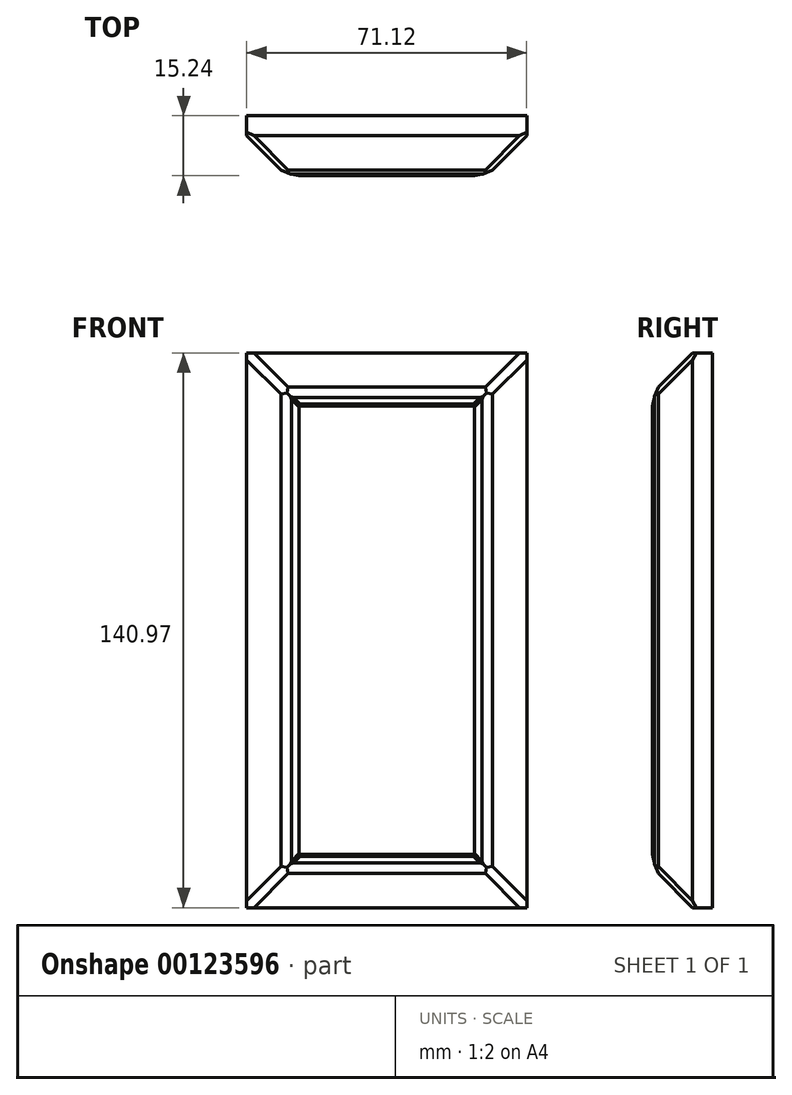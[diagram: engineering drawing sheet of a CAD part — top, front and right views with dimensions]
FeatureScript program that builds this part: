
annotation { "Feature Type Name" : "Feature", "Feature Type Description" : "" }
export const myFeature = defineFeature(function(context is Context, id is Id, definition is map)
    precondition{}
    {
        {
            var Q0;
            Q0=qCreatedBy(makeId("Front.planeOp"),FACE);
            var sketch = newSketch(context, id + "F0", { "sketchPlane" : qUnion([Q0])});
            skLineSegment(sketch, "E0.bottom", {"start": v(-36.8, 94.4) * mm, "end": v(34.31, 94.4) * mm});
            skLineSegment(sketch, "E0.top", {"start": v(-36.8, -46.57) * mm, "end": v(34.31, -46.57) * mm});
            skLineSegment(sketch, "E0.left", {"start": v(-36.8, 94.4) * mm, "end": v(-36.8, -46.57) * mm});
            skLineSegment(sketch, "E0.right", {"start": v(34.31, 94.4) * mm, "end": v(34.31, -46.57) * mm});
            skSolve(sketch);
        }
        {
            var Q0;
            Q0 = qSketchRegion(id + "F0", true);
            extrude(context, id + "F1", {"entities" : qUnion([Q0]), "depth" : 15.24 * mm});
        }
        {
            var Q0;
            Q0=makeQuery(id+"F1.opExtrude","CAP_EDGE",EDGE,{"disambiguationData":[OSD([sQuery(id+"F0.wireOp",EDGE,"E0.bottom")])],"isStart":false});
            var Q1;
            Q1=makeQuery(id+"F1.opExtrude","CAP_EDGE",EDGE,{"disambiguationData":[OSD([sQuery(id+"F0.wireOp",EDGE,"E0.right")])],"isStart":false});
            var Q2;
            Q2=makeQuery(id+"F1.opExtrude","CAP_EDGE",EDGE,{"disambiguationData":[OSD([sQuery(id+"F0.wireOp",EDGE,"E0.left")])],"isStart":false});
            var Q3;
            Q3=makeQuery(id+"F1.opExtrude","CAP_EDGE",EDGE,{"disambiguationData":[OSD([sQuery(id+"F0.wireOp",EDGE,"E0.top")])],"isStart":false});
            chamfer(context, id + "F2", {"entities" : qUnion([Q0, Q1, Q2, Q3]), "width" : 10.16 * mm, "tangentPropagation" : true});
        }
        {
            var Q0;
            {var subQ0=sQuery(id+"F0.wireOp",EDGE,"E0.left");Q0=makeQuery(id+"F2.opChamfer","BLEND_EDGE",EDGE,{"blendedFrom":[makeQuery(id+"F1.opExtrude","CAP_EDGE",EDGE,{"disambiguationData":[OSD([subQ0])],"isStart":false}),makeQuery(id+"F1.opExtrude","CAP_FACE",FACE,{"disambiguationData":[OSD([sQuery(id+"F0.wireOp",EDGE,"E0.bottom"),sQuery(id+"F0.wireOp",EDGE,"E0.top"),subQ0,sQuery(id+"F0.wireOp",EDGE,"E0.right")])],"isStart":false})],"blendedInto":[makeQuery(id+"F1.opExtrude","CAP_FACE",FACE,{"disambiguationData":[OSD([sQuery(id+"F0.wireOp",EDGE,"E0.bottom"),sQuery(id+"F0.wireOp",EDGE,"E0.top"),subQ0,sQuery(id+"F0.wireOp",EDGE,"E0.right")])],"isStart":false})]});}
            var Q1;
            {var subQ0=sQuery(id+"F0.wireOp",EDGE,"E0.top");Q1=makeQuery(id+"F2.opChamfer","BLEND_EDGE",EDGE,{"blendedFrom":[makeQuery(id+"F1.opExtrude","CAP_EDGE",EDGE,{"disambiguationData":[OSD([subQ0])],"isStart":false}),makeQuery(id+"F1.opExtrude","CAP_FACE",FACE,{"disambiguationData":[OSD([sQuery(id+"F0.wireOp",EDGE,"E0.bottom"),subQ0,sQuery(id+"F0.wireOp",EDGE,"E0.left"),sQuery(id+"F0.wireOp",EDGE,"E0.right")])],"isStart":false})],"blendedInto":[makeQuery(id+"F1.opExtrude","CAP_FACE",FACE,{"disambiguationData":[OSD([sQuery(id+"F0.wireOp",EDGE,"E0.bottom"),subQ0,sQuery(id+"F0.wireOp",EDGE,"E0.left"),sQuery(id+"F0.wireOp",EDGE,"E0.right")])],"isStart":false})]});}
            var Q2;
            {var subQ0=sQuery(id+"F0.wireOp",EDGE,"E0.right");Q2=makeQuery(id+"F2.opChamfer","BLEND_EDGE",EDGE,{"blendedFrom":[makeQuery(id+"F1.opExtrude","CAP_EDGE",EDGE,{"disambiguationData":[OSD([subQ0])],"isStart":false}),makeQuery(id+"F1.opExtrude","CAP_FACE",FACE,{"disambiguationData":[OSD([sQuery(id+"F0.wireOp",EDGE,"E0.bottom"),sQuery(id+"F0.wireOp",EDGE,"E0.top"),sQuery(id+"F0.wireOp",EDGE,"E0.left"),subQ0])],"isStart":false})],"blendedInto":[makeQuery(id+"F1.opExtrude","CAP_FACE",FACE,{"disambiguationData":[OSD([sQuery(id+"F0.wireOp",EDGE,"E0.bottom"),sQuery(id+"F0.wireOp",EDGE,"E0.top"),sQuery(id+"F0.wireOp",EDGE,"E0.left"),subQ0])],"isStart":false})]});}
            var Q3;
            {var subQ0=sQuery(id+"F0.wireOp",EDGE,"E0.bottom");Q3=makeQuery(id+"F2.opChamfer","BLEND_EDGE",EDGE,{"blendedFrom":[makeQuery(id+"F1.opExtrude","CAP_EDGE",EDGE,{"disambiguationData":[OSD([subQ0])],"isStart":false}),makeQuery(id+"F1.opExtrude","CAP_FACE",FACE,{"disambiguationData":[OSD([subQ0,sQuery(id+"F0.wireOp",EDGE,"E0.top"),sQuery(id+"F0.wireOp",EDGE,"E0.left"),sQuery(id+"F0.wireOp",EDGE,"E0.right")])],"isStart":false})],"blendedInto":[makeQuery(id+"F1.opExtrude","CAP_FACE",FACE,{"disambiguationData":[OSD([subQ0,sQuery(id+"F0.wireOp",EDGE,"E0.top"),sQuery(id+"F0.wireOp",EDGE,"E0.left"),sQuery(id+"F0.wireOp",EDGE,"E0.right")])],"isStart":false})]});}
            chamfer(context, id + "F3", {"entities" : qUnion([Q0, Q1, Q2, Q3]), "width" : 5.08 * mm, "tangentPropagation" : true});
        }
        {
            var Q0;
            {var subQ0=sQuery(id+"F0.wireOp",EDGE,"E0.bottom");var subQ1=makeQuery(id+"F1.opExtrude","CAP_FACE",FACE,{"disambiguationData":[OSD([subQ0,sQuery(id+"F0.wireOp",EDGE,"E0.top"),sQuery(id+"F0.wireOp",EDGE,"E0.left"),sQuery(id+"F0.wireOp",EDGE,"E0.right")])],"isStart":false});Q0=makeQuery(id+"F3.opChamfer","BLEND_EDGE",EDGE,{"blendedFrom":[makeQuery(id+"F2.opChamfer","BLEND_EDGE",EDGE,{"blendedFrom":[makeQuery(id+"F1.opExtrude","CAP_EDGE",EDGE,{"disambiguationData":[OSD([subQ0])],"isStart":false}),subQ1],"blendedInto":[subQ1]}),subQ1],"blendedInto":[subQ1]});}
            var Q1;
            {var subQ0=sQuery(id+"F0.wireOp",EDGE,"E0.top");var subQ1=makeQuery(id+"F1.opExtrude","CAP_FACE",FACE,{"disambiguationData":[OSD([sQuery(id+"F0.wireOp",EDGE,"E0.bottom"),subQ0,sQuery(id+"F0.wireOp",EDGE,"E0.left"),sQuery(id+"F0.wireOp",EDGE,"E0.right")])],"isStart":false});Q1=makeQuery(id+"F3.opChamfer","BLEND_EDGE",EDGE,{"blendedFrom":[makeQuery(id+"F2.opChamfer","BLEND_EDGE",EDGE,{"blendedFrom":[makeQuery(id+"F1.opExtrude","CAP_EDGE",EDGE,{"disambiguationData":[OSD([subQ0])],"isStart":false}),subQ1],"blendedInto":[subQ1]}),subQ1],"blendedInto":[subQ1]});}
            var Q2;
            {var subQ0=sQuery(id+"F0.wireOp",EDGE,"E0.left");var subQ1=makeQuery(id+"F1.opExtrude","CAP_FACE",FACE,{"disambiguationData":[OSD([sQuery(id+"F0.wireOp",EDGE,"E0.bottom"),sQuery(id+"F0.wireOp",EDGE,"E0.top"),subQ0,sQuery(id+"F0.wireOp",EDGE,"E0.right")])],"isStart":false});Q2=makeQuery(id+"F3.opChamfer","BLEND_EDGE",EDGE,{"blendedFrom":[makeQuery(id+"F2.opChamfer","BLEND_EDGE",EDGE,{"blendedFrom":[makeQuery(id+"F1.opExtrude","CAP_EDGE",EDGE,{"disambiguationData":[OSD([subQ0])],"isStart":false}),subQ1],"blendedInto":[subQ1]}),subQ1],"blendedInto":[subQ1]});}
            var Q3;
            {var subQ0=sQuery(id+"F0.wireOp",EDGE,"E0.right");var subQ1=makeQuery(id+"F1.opExtrude","CAP_FACE",FACE,{"disambiguationData":[OSD([sQuery(id+"F0.wireOp",EDGE,"E0.bottom"),sQuery(id+"F0.wireOp",EDGE,"E0.top"),sQuery(id+"F0.wireOp",EDGE,"E0.left"),subQ0])],"isStart":false});Q3=makeQuery(id+"F3.opChamfer","BLEND_EDGE",EDGE,{"blendedFrom":[makeQuery(id+"F2.opChamfer","BLEND_EDGE",EDGE,{"blendedFrom":[makeQuery(id+"F1.opExtrude","CAP_EDGE",EDGE,{"disambiguationData":[OSD([subQ0])],"isStart":false}),subQ1],"blendedInto":[subQ1]}),subQ1],"blendedInto":[subQ1]});}
            chamfer(context, id + "F4", {"entities" : qUnion([Q0, Q1, Q2, Q3]), "width" : 5.08 * mm, "tangentPropagation" : true});
        }
        {
            var Q0;
            {var subQ0=sQuery(id+"F0.wireOp",EDGE,"E0.right");var subQ1=sQuery(id+"F0.wireOp",EDGE,"E0.bottom");var subQ2=makeQuery(id+"F1.opExtrude","CAP_FACE",FACE,{"disambiguationData":[OSD([subQ1,sQuery(id+"F0.wireOp",EDGE,"E0.top"),sQuery(id+"F0.wireOp",EDGE,"E0.left"),subQ0])],"isStart":false});var subQ3=subQ2;Q0=makeQuery(id+"F4.opChamfer","BLEND_EDGE",EDGE,{"blendedFrom":[makeQuery(id+"F3.opChamfer","BLEND_EDGE",EDGE,{"blendedFrom":[makeQuery(id+"F2.opChamfer","BLEND_EDGE",EDGE,{"blendedFrom":[makeQuery(id+"F1.opExtrude","CAP_EDGE",EDGE,{"disambiguationData":[OSD([subQ1])],"isStart":false}),subQ2],"blendedInto":[subQ2]}),subQ3],"blendedInto":[subQ3]}),makeQuery(id+"F3.opChamfer","BLEND_EDGE",EDGE,{"blendedFrom":[makeQuery(id+"F2.opChamfer","BLEND_EDGE",EDGE,{"blendedFrom":[makeQuery(id+"F1.opExtrude","CAP_EDGE",EDGE,{"disambiguationData":[OSD([subQ0])],"isStart":false}),subQ2],"blendedInto":[subQ2]}),subQ3],"blendedInto":[subQ3]})],"blendedInto":[]});}
            var Q1;
            {var subQ0=sQuery(id+"F0.wireOp",EDGE,"E0.left");var subQ1=sQuery(id+"F0.wireOp",EDGE,"E0.bottom");var subQ2=makeQuery(id+"F1.opExtrude","CAP_FACE",FACE,{"disambiguationData":[OSD([subQ1,sQuery(id+"F0.wireOp",EDGE,"E0.top"),subQ0,sQuery(id+"F0.wireOp",EDGE,"E0.right")])],"isStart":false});var subQ3=subQ2;Q1=makeQuery(id+"F4.opChamfer","BLEND_EDGE",EDGE,{"blendedFrom":[makeQuery(id+"F3.opChamfer","BLEND_EDGE",EDGE,{"blendedFrom":[makeQuery(id+"F2.opChamfer","BLEND_EDGE",EDGE,{"blendedFrom":[makeQuery(id+"F1.opExtrude","CAP_EDGE",EDGE,{"disambiguationData":[OSD([subQ1])],"isStart":false}),subQ2],"blendedInto":[subQ2]}),subQ3],"blendedInto":[subQ3]}),makeQuery(id+"F3.opChamfer","BLEND_EDGE",EDGE,{"blendedFrom":[makeQuery(id+"F2.opChamfer","BLEND_EDGE",EDGE,{"blendedFrom":[makeQuery(id+"F1.opExtrude","CAP_EDGE",EDGE,{"disambiguationData":[OSD([subQ0])],"isStart":false}),subQ2],"blendedInto":[subQ2]}),subQ3],"blendedInto":[subQ3]})],"blendedInto":[]});}
            var Q2;
            {var subQ0=sQuery(id+"F0.wireOp",EDGE,"E0.left");var subQ1=sQuery(id+"F0.wireOp",EDGE,"E0.top");var subQ2=makeQuery(id+"F1.opExtrude","CAP_FACE",FACE,{"disambiguationData":[OSD([sQuery(id+"F0.wireOp",EDGE,"E0.bottom"),subQ1,subQ0,sQuery(id+"F0.wireOp",EDGE,"E0.right")])],"isStart":false});var subQ3=subQ2;Q2=makeQuery(id+"F4.opChamfer","BLEND_EDGE",EDGE,{"blendedFrom":[makeQuery(id+"F3.opChamfer","BLEND_EDGE",EDGE,{"blendedFrom":[makeQuery(id+"F2.opChamfer","BLEND_EDGE",EDGE,{"blendedFrom":[makeQuery(id+"F1.opExtrude","CAP_EDGE",EDGE,{"disambiguationData":[OSD([subQ1])],"isStart":false}),subQ2],"blendedInto":[subQ2]}),subQ3],"blendedInto":[subQ3]}),makeQuery(id+"F3.opChamfer","BLEND_EDGE",EDGE,{"blendedFrom":[makeQuery(id+"F2.opChamfer","BLEND_EDGE",EDGE,{"blendedFrom":[makeQuery(id+"F1.opExtrude","CAP_EDGE",EDGE,{"disambiguationData":[OSD([subQ0])],"isStart":false}),subQ2],"blendedInto":[subQ2]}),subQ3],"blendedInto":[subQ3]})],"blendedInto":[]});}
            var Q3;
            {var subQ0=sQuery(id+"F0.wireOp",EDGE,"E0.right");var subQ1=sQuery(id+"F0.wireOp",EDGE,"E0.top");var subQ2=makeQuery(id+"F1.opExtrude","CAP_FACE",FACE,{"disambiguationData":[OSD([sQuery(id+"F0.wireOp",EDGE,"E0.bottom"),subQ1,sQuery(id+"F0.wireOp",EDGE,"E0.left"),subQ0])],"isStart":false});var subQ3=subQ2;Q3=makeQuery(id+"F4.opChamfer","BLEND_EDGE",EDGE,{"blendedFrom":[makeQuery(id+"F3.opChamfer","BLEND_EDGE",EDGE,{"blendedFrom":[makeQuery(id+"F2.opChamfer","BLEND_EDGE",EDGE,{"blendedFrom":[makeQuery(id+"F1.opExtrude","CAP_EDGE",EDGE,{"disambiguationData":[OSD([subQ1])],"isStart":false}),subQ2],"blendedInto":[subQ2]}),subQ3],"blendedInto":[subQ3]}),makeQuery(id+"F3.opChamfer","BLEND_EDGE",EDGE,{"blendedFrom":[makeQuery(id+"F2.opChamfer","BLEND_EDGE",EDGE,{"blendedFrom":[makeQuery(id+"F1.opExtrude","CAP_EDGE",EDGE,{"disambiguationData":[OSD([subQ0])],"isStart":false}),subQ2],"blendedInto":[subQ2]}),subQ3],"blendedInto":[subQ3]})],"blendedInto":[]});}
            chamfer(context, id + "F5", {"entities" : qUnion([Q0, Q1, Q2, Q3]), "width" : 2.54 * mm, "tangentPropagation" : true});
        }
        {
            var Q0;
            {var subQ0=sQuery(id+"F0.wireOp",EDGE,"E0.bottom");var subQ1=makeQuery(id+"F1.opExtrude","CAP_FACE",FACE,{"disambiguationData":[OSD([subQ0,sQuery(id+"F0.wireOp",EDGE,"E0.top"),sQuery(id+"F0.wireOp",EDGE,"E0.left"),sQuery(id+"F0.wireOp",EDGE,"E0.right")])],"isStart":false});var subQ2=subQ1;Q0=makeQuery(id+"F4.opChamfer","BLEND_EDGE",EDGE,{"blendedFrom":[makeQuery(id+"F3.opChamfer","BLEND_EDGE",EDGE,{"blendedFrom":[makeQuery(id+"F2.opChamfer","BLEND_EDGE",EDGE,{"blendedFrom":[makeQuery(id+"F1.opExtrude","CAP_EDGE",EDGE,{"disambiguationData":[OSD([subQ0])],"isStart":false}),subQ1],"blendedInto":[subQ1]}),subQ2],"blendedInto":[subQ2]}),subQ2],"blendedInto":[subQ2]});}
            var Q1;
            {var subQ0=sQuery(id+"F0.wireOp",EDGE,"E0.top");var subQ1=makeQuery(id+"F1.opExtrude","CAP_FACE",FACE,{"disambiguationData":[OSD([sQuery(id+"F0.wireOp",EDGE,"E0.bottom"),subQ0,sQuery(id+"F0.wireOp",EDGE,"E0.left"),sQuery(id+"F0.wireOp",EDGE,"E0.right")])],"isStart":false});var subQ2=subQ1;Q1=makeQuery(id+"F4.opChamfer","BLEND_EDGE",EDGE,{"blendedFrom":[makeQuery(id+"F3.opChamfer","BLEND_EDGE",EDGE,{"blendedFrom":[makeQuery(id+"F2.opChamfer","BLEND_EDGE",EDGE,{"blendedFrom":[makeQuery(id+"F1.opExtrude","CAP_EDGE",EDGE,{"disambiguationData":[OSD([subQ0])],"isStart":false}),subQ1],"blendedInto":[subQ1]}),subQ2],"blendedInto":[subQ2]}),subQ2],"blendedInto":[subQ2]});}
            chamfer(context, id + "F6", {"entities" : qUnion([Q0, Q1]), "width" : 2.54 * mm, "tangentPropagation" : true});
        }
        {
            var Q0;
            Q0=makeQuery(id+"F2.opChamfer","BLEND_EDGE",EDGE,{"blendedFrom":[makeQuery(id+"F1.opExtrude","CAP_EDGE",EDGE,{"disambiguationData":[OSD([sQuery(id+"F0.wireOp",EDGE,"E0.top")])],"isStart":false}),makeQuery(id+"F1.opExtrude","CAP_EDGE",EDGE,{"disambiguationData":[OSD([sQuery(id+"F0.wireOp",EDGE,"E0.right")])],"isStart":false})],"blendedInto":[]});
            var Q1;
            Q1=makeQuery(id+"F2.opChamfer","BLEND_EDGE",EDGE,{"blendedFrom":[makeQuery(id+"F1.opExtrude","CAP_EDGE",EDGE,{"disambiguationData":[OSD([sQuery(id+"F0.wireOp",EDGE,"E0.bottom")])],"isStart":false}),makeQuery(id+"F1.opExtrude","CAP_EDGE",EDGE,{"disambiguationData":[OSD([sQuery(id+"F0.wireOp",EDGE,"E0.right")])],"isStart":false})],"blendedInto":[]});
            var Q2;
            Q2=makeQuery(id+"F2.opChamfer","BLEND_EDGE",EDGE,{"blendedFrom":[makeQuery(id+"F1.opExtrude","CAP_EDGE",EDGE,{"disambiguationData":[OSD([sQuery(id+"F0.wireOp",EDGE,"E0.bottom")])],"isStart":false}),makeQuery(id+"F1.opExtrude","CAP_EDGE",EDGE,{"disambiguationData":[OSD([sQuery(id+"F0.wireOp",EDGE,"E0.left")])],"isStart":false})],"blendedInto":[]});
            var Q3;
            Q3=makeQuery(id+"F2.opChamfer","BLEND_EDGE",EDGE,{"blendedFrom":[makeQuery(id+"F1.opExtrude","CAP_EDGE",EDGE,{"disambiguationData":[OSD([sQuery(id+"F0.wireOp",EDGE,"E0.top")])],"isStart":false}),makeQuery(id+"F1.opExtrude","CAP_EDGE",EDGE,{"disambiguationData":[OSD([sQuery(id+"F0.wireOp",EDGE,"E0.left")])],"isStart":false})],"blendedInto":[]});
            chamfer(context, id + "F7", {"entities" : qUnion([Q0, Q1, Q2, Q3]), "width" : 2.54 * mm, "tangentPropagation" : true});
        }
    });
